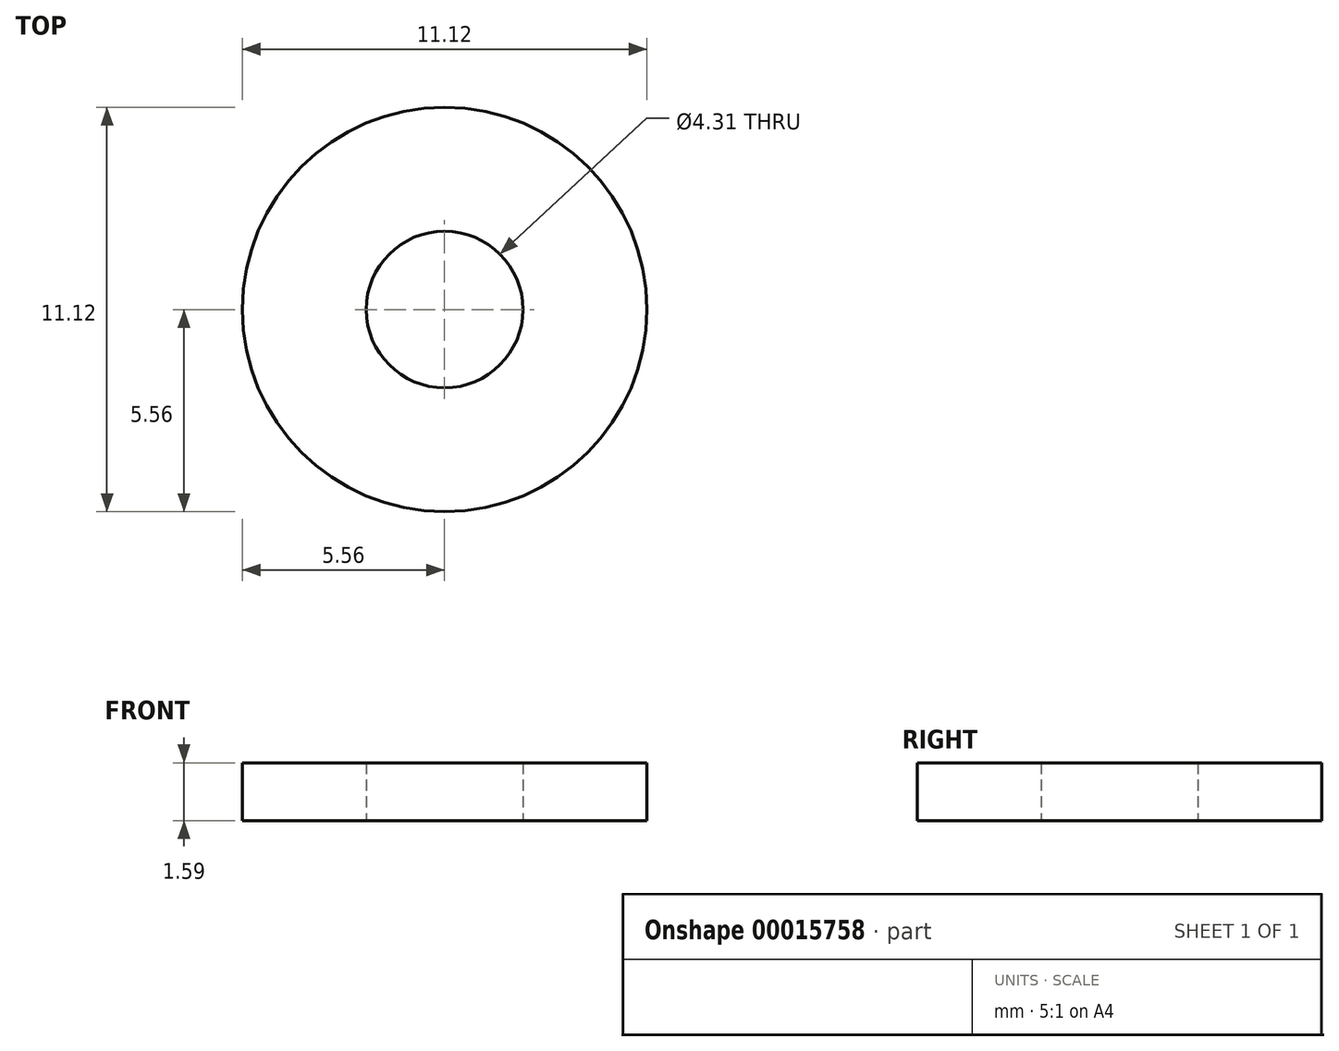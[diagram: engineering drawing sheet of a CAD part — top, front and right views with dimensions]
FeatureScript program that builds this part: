
annotation { "Feature Type Name" : "Feature", "Feature Type Description" : "" }
export const myFeature = defineFeature(function(context is Context, id is Id, definition is map)
    precondition{}
    {
        {
            var Q0;
            Q0=qCreatedBy(makeId("Top.planeOp"),FACE);
            var sketch = newSketch(context, id + "F0", { "sketchPlane" : qUnion([Q0])});
            skCircle(sketch, "E0", {"center": v(0, 0) * mm, "radius": 2.15 * mm});
            skCircle(sketch, "E1", {"center": v(0, 0) * mm, "radius": 5.56 * mm});
            skSolve(sketch);
        }
        {
            var Q0;
            Q0 = qSketchRegion(id + "F0", true);
            extrude(context, id + "F1", {"entities" : qUnion([Q0]), "depth" : 1.59 * mm});
        }
    });
